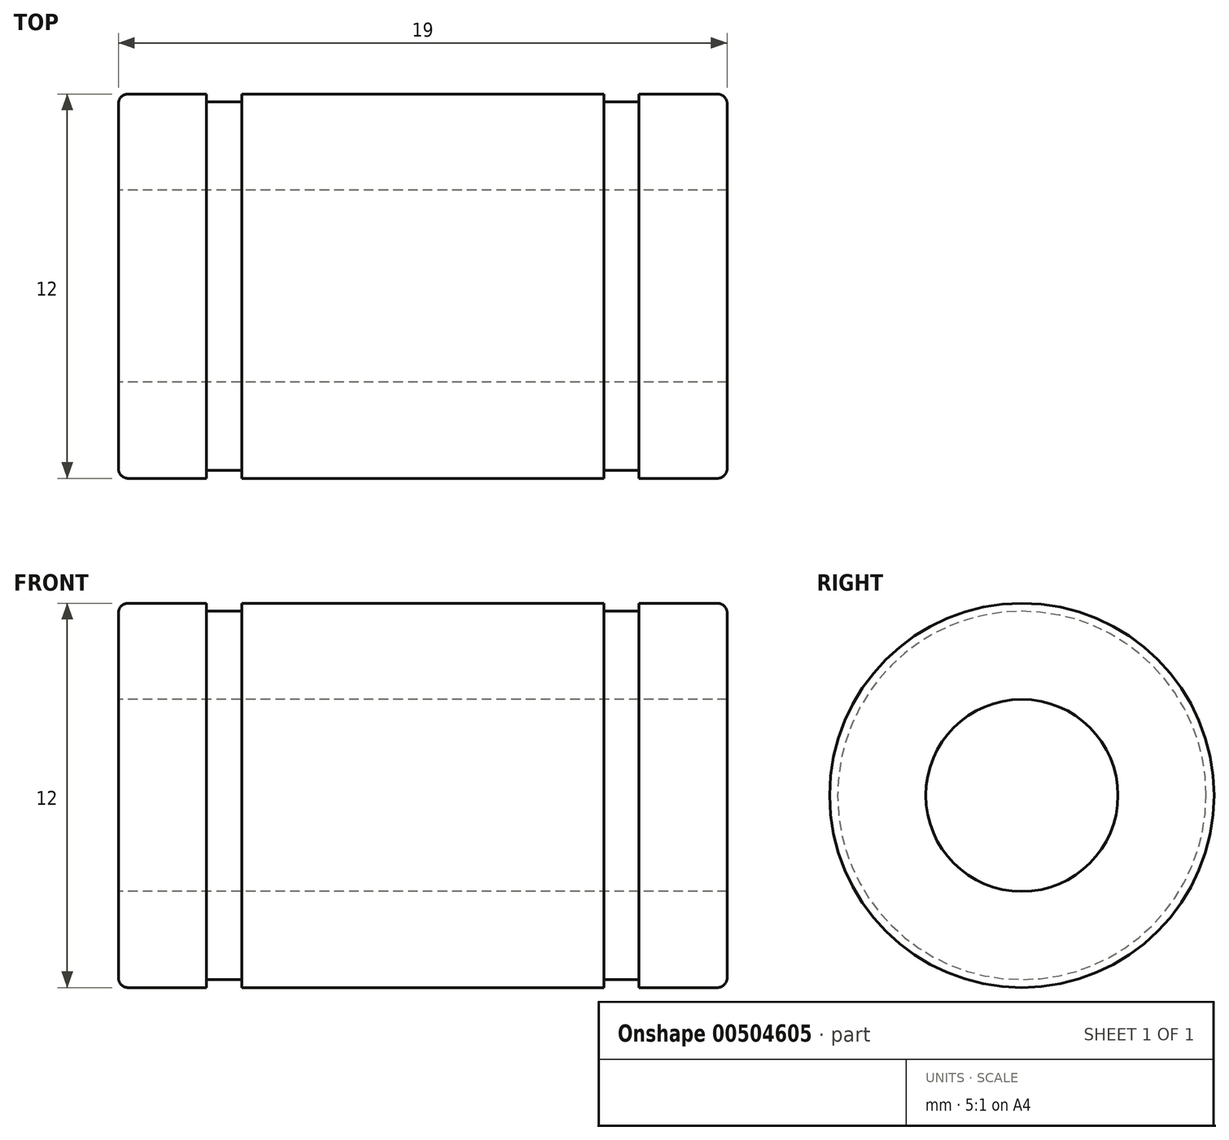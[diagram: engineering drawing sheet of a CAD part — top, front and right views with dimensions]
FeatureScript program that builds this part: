
annotation { "Feature Type Name" : "Feature", "Feature Type Description" : "" }
export const myFeature = defineFeature(function(context is Context, id is Id, definition is map)
    precondition{}
    {
        {
            assignVariable(context, id + "F0", {"name" : "D", "anyValue" : 12 * mm});
        }
        {
            var Q0;
            Q0=qCreatedBy(makeId("Front.planeOp"),FACE);
            var sketch = newSketch(context, id + "F1", { "sketchPlane" : qUnion([Q0])});
            skLineSegment(sketch, "E0", {"start": v(-9.5, 0) * mm, "end": v(9.5, 0) * mm, "construction": true});
            skLineSegment(sketch, "E1", {"start": v(-9.5, 3) * mm, "end": v(9.5, 3) * mm});
            skLineSegment(sketch, "E2", {"start": v(9.5, 3) * mm, "end": v(9.5, 6) * mm});
            skLineSegment(sketch, "E3", {"start": v(9.5, 6) * mm, "end": v(6.75, 6) * mm});
            skLineSegment(sketch, "E4", {"start": v(6.75, 6) * mm, "end": v(6.75, 5.75) * mm});
            skLineSegment(sketch, "E5", {"start": v(6.75, 5.75) * mm, "end": v(5.65, 5.75) * mm});
            skLineSegment(sketch, "E6", {"start": v(5.65, 5.75) * mm, "end": v(5.65, 6) * mm});
            skLineSegment(sketch, "E7", {"start": v(5.65, 6) * mm, "end": v(-5.65, 6) * mm});
            skLineSegment(sketch, "E8", {"start": v(-5.65, 6) * mm, "end": v(-5.65, 5.75) * mm});
            skLineSegment(sketch, "E9", {"start": v(-5.65, 5.75) * mm, "end": v(-6.75, 5.75) * mm});
            skLineSegment(sketch, "E10", {"start": v(-6.75, 5.75) * mm, "end": v(-6.75, 6) * mm});
            skLineSegment(sketch, "E11", {"start": v(-6.75, 6) * mm, "end": v(-9.5, 6) * mm});
            skLineSegment(sketch, "E12", {"start": v(-9.5, 6) * mm, "end": v(-9.5, 3) * mm});
            skSolve(sketch);
        }
        {
            var Q0;
            Q0=qSketchRegion(id+"F1",true);
            var Q1;
            Q1=sQuery(id+"F1.wireOp",EDGE,"E0");
            revolve(context, id + "F2", {"entities" : qUnion([Q0]), "axis" : qUnion([Q1]), "revolveType" : RevolveType.FULL});
        }
        {
            var Q0;
            Q0=makeQuery(id+"F2.opRevolve","SWEPT_EDGE",EDGE,{"disambiguationData":[OSD([sQuery(id+"F1.wireOp",EDGE,"E11"),sQuery(id+"F1.wireOp",EDGE,"E12")])]});
            var Q1;
            Q1=makeQuery(id+"F2.opRevolve","SWEPT_EDGE",EDGE,{"disambiguationData":[OSD([sQuery(id+"F1.wireOp",EDGE,"E2"),sQuery(id+"F1.wireOp",EDGE,"E3")])]});
            fillet(context, id + "F3", {"entities" : qUnion([Q0, Q1]), "radius" : getVariable(context, 'D') * 0.03, "tangentPropagation" : true, "allowEdgeOverflow" : false});
        }
    });
